# Revit family: Door-Industrial_Door-Dynaco-D-310
name_source: partatom
category: Doors
revit_build: Autodesk Revit 2016 (Build: 20150714_1515(x64)
units: mm (PartAtom-declared; Revit-internal decimal feet)

## family parameters
Always vertical = Yes
Cut with Voids When Loaded = No
Host = Wall
Room Calculation Point = No
Shared = No

## types (2) — shared parameters
Air permeability, EN 12426 = class 1 (24 m3/m2/h at 50 Pa)
/m2
/h at 50 Pa)
Analytic Construction = <None>
BIMobject category = Industrial Doors
C1 = Yes
C2 = Yes
C3 = Yes
C4 = Yes
Closing Speed = 1,0 m/s
Control Parameter = 130 mm  [stored 0.426509 ft]
Control Unit = Yes
Date of publishing = 2015-10-01
Depth = 0.00
Design country = Belgium
Door Curtain Material = PVC_Dynaco_RAL 1003_Signal Yellow
Edition number = 1
Four Column Windows = Yes
IFC Classification = Door
Lifetime expectations = 1.000.000 cycles
Manufacturer country = Belgium
Manufacturer name = Entrematic
Material main = PVC
Material secondary = Steel
NBS Reference Code = 59-23-38
NBS Reference Description = High Speed Doorsets
Nominal height = 400000
Nominal width = 400000
One Column Windows = No
One Row Windows = No
Opening Speed = up to 1,0 m/s 2
Product Guid = b3fc8bd1-5c73-4920-90bc-5e452dc74115
Product SKU = dyn-d310
Product data url = https://bimobject.com
Product family = High speed door
Product group = Inside door
QR code = http://bimobject.com
R1 = Yes
R2 = Yes
R3 = Yes
Technical description = https://www.dynacodoor.com
Thermal transmittance = 6,02 W/ (m2 K)
K)
Three Column Windows = No
Three Row Windows = Yes
Top Cover = 500 mm  [stored 1.64042 ft]
Two Column Windows = No
Two Row Windows = No
UNSPSC Code = 301715
Uniclass 1.4 Code = L411
Uniclass 1.4 Description = Doors
Uniclass 2.0 Code = PR-59-23-38
Uniclass 2.0 Description = High Speed Doorsets
Water penetration, EN 12425 = class 2 (50 N/m2)
)
Wind load resistance,EN 12424 = class 1 (300 N/m2)maximum wind load while closing 50 N/m2
)
zero-valued in all types: Opening Height, Weight Net (Kg)

## per-type parameters (varying)
| type | Min Height of panel | Name of the object | Option 1 | Vision Panel | Vision Panel Height (400,800) | Vision Panel Min Height | Vision panel height from bottom |
| Dynaco_D-310_800 | 900 mm  [stored 2.95276 ft] | Crawford HS9010G high speed door | Galvanized steel | 800 | 800 mm  [stored 2.62467 ft] | 1000 mm  [stored 3.28084 ft] | 1000 mm  [stored 3.28084 ft] |
| Dynaco_D-310_400 | 700 mm  [stored 2.29659 ft] |  | Stainless steel | 400 | 400 mm  [stored 1.31234 ft] | 700 mm  [stored 2.29659 ft] | 600 mm |

note: [stored X ft] marks values corroborated as IEEE doubles in the binary element streams (Revit-internal decimal feet)

## geometry (parser evidence)
native form markers: Blend x4, Sweep x29
no freeform markers — native parametric forms only
